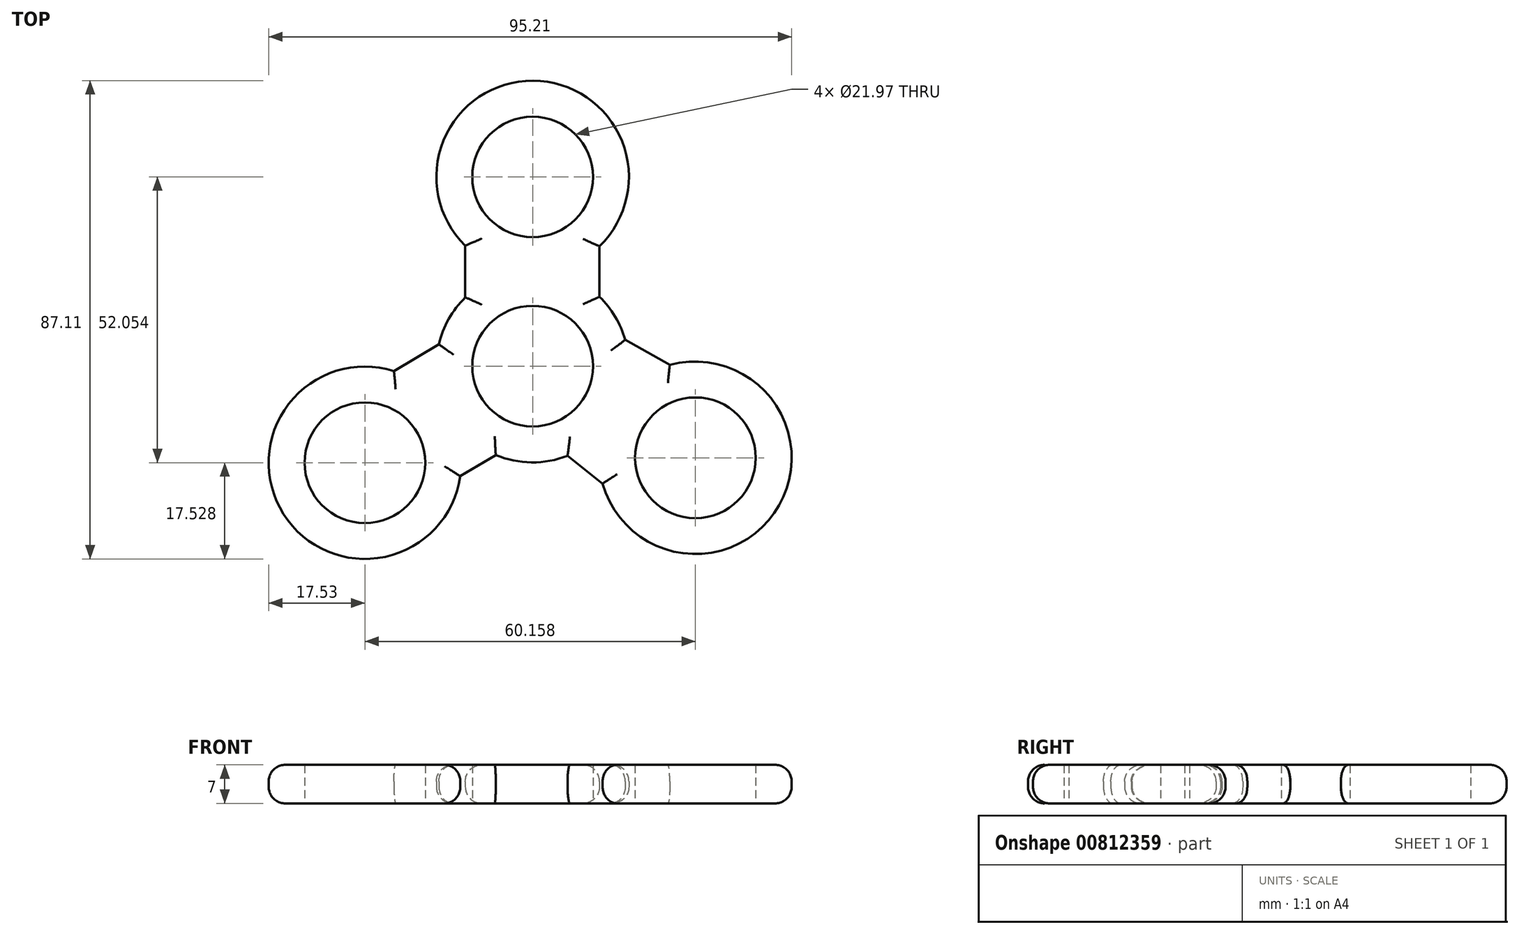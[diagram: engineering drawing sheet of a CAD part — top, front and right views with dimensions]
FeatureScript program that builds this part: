
annotation { "Feature Type Name" : "Feature", "Feature Type Description" : "" }
export const myFeature = defineFeature(function(context is Context, id is Id, definition is map)
    precondition{}
    {
        {
            var Q0;
            Q0=qCreatedBy(makeId("Top.planeOp"),FACE);
            var sketch = newSketch(context, id + "F0", { "sketchPlane" : qUnion([Q0])});
            skCircle(sketch, "E0", {"center": v(0, 0) * mm, "radius": 10.99 * mm});
            skCircle(sketch, "E1", {"center": v(0, 34.46) * mm, "radius": 10.99 * mm});
            skCircle(sketch, "E2", {"center": v(29.63, -16.69) * mm, "radius": 10.99 * mm});
            skCircle(sketch, "E3", {"center": v(-30.53, -17.6) * mm, "radius": 10.99 * mm});
            skArc(sketch, "E4", {"start": v(12.74, -21.39) * mm, "mid": v(44.88, -25.33) * mm, "end": v(24.97, 0.2) * mm});
            skArc(sketch, "E5", {"start": v(-25.26, -0.88) * mm, "mid": v(-45.36, -26.94) * mm, "end": v(-13.18, -20.04) * mm});
            skArc(sketch, "E6", {"start": v(12.16, 21.84) * mm, "mid": v(0.07, 51.99) * mm, "end": v(-12.26, 21.94) * mm});
            skArc(sketch, "E7", {"start": v(-6.71, -16.19) * mm, "mid": v(-0.2, -17.52) * mm, "end": v(6.35, -16.33) * mm});
            skLineSegment(sketch, "E8", {"start": v(-12.26, 21.94) * mm, "end": v(-12.26, 12.52) * mm});
            skLineSegment(sketch, "E9", {"start": v(12.16, 21.84) * mm, "end": v(12.16, 12.62) * mm});
            skLineSegment(sketch, "E10", {"start": v(-25.26, -0.88) * mm, "end": v(-17.07, 3.97) * mm});
            skLineSegment(sketch, "E11", {"start": v(-13.18, -20.04) * mm, "end": v(-6.71, -16.19) * mm});
            skLineSegment(sketch, "E12", {"start": v(16.86, 4.8) * mm, "end": v(24.97, 0.2) * mm});
            skLineSegment(sketch, "E13", {"start": v(6.35, -16.33) * mm, "end": v(12.74, -21.39) * mm});
            skArc(sketch, "E14.trimOffspring", {"start": v(-12.26, 12.52) * mm, "mid": v(-15.28, 8.6) * mm, "end": v(-17.07, 3.97) * mm});
            skArc(sketch, "E15.trimOffspring", {"start": v(16.86, 4.8) * mm, "mid": v(15.03, 9.02) * mm, "end": v(12.16, 12.62) * mm});
            skSolve(sketch);
        }
        {
            var Q0;
            Q0 = qSketchRegion(id + "F0", true);
            extrude(context, id + "F1", {"entities" : qUnion([Q0]), "depth" : 7 * mm, "offsetDistance" : 25.4 * mm});
        }
        {
            var Q0;
            Q0=makeQuery(id+"F1.opExtrude","CAP_EDGE",EDGE,{"disambiguationData":[OSD([sQuery(id+"F0.wireOp",EDGE,"E6")])],"isStart":true});
            var Q1;
            Q1=makeQuery(id+"F1.opExtrude","CAP_EDGE",EDGE,{"disambiguationData":[OSD([sQuery(id+"F0.wireOp",EDGE,"E9")])],"isStart":true});
            var Q2;
            Q2=makeQuery(id+"F1.opExtrude","CAP_EDGE",EDGE,{"disambiguationData":[OSD([sQuery(id+"F0.wireOp",EDGE,"E15.trimOffspring")])],"isStart":true});
            var Q3;
            Q3=makeQuery(id+"F1.opExtrude","CAP_EDGE",EDGE,{"disambiguationData":[OSD([sQuery(id+"F0.wireOp",EDGE,"E12")])],"isStart":true});
            var Q4;
            Q4=makeQuery(id+"F1.opExtrude","CAP_EDGE",EDGE,{"disambiguationData":[OSD([sQuery(id+"F0.wireOp",EDGE,"E4")])],"isStart":true});
            var Q5;
            Q5=makeQuery(id+"F1.opExtrude","CAP_EDGE",EDGE,{"disambiguationData":[OSD([sQuery(id+"F0.wireOp",EDGE,"E13")])],"isStart":true});
            var Q6;
            Q6=makeQuery(id+"F1.opExtrude","CAP_EDGE",EDGE,{"disambiguationData":[OSD([sQuery(id+"F0.wireOp",EDGE,"E7")])],"isStart":true});
            var Q7;
            Q7=makeQuery(id+"F1.opExtrude","CAP_EDGE",EDGE,{"disambiguationData":[OSD([sQuery(id+"F0.wireOp",EDGE,"E11")])],"isStart":true});
            var Q8;
            Q8=makeQuery(id+"F1.opExtrude","CAP_EDGE",EDGE,{"disambiguationData":[OSD([sQuery(id+"F0.wireOp",EDGE,"E5")])],"isStart":true});
            var Q9;
            Q9=makeQuery(id+"F1.opExtrude","CAP_EDGE",EDGE,{"disambiguationData":[OSD([sQuery(id+"F0.wireOp",EDGE,"E10")])],"isStart":true});
            var Q10;
            Q10=makeQuery(id+"F1.opExtrude","CAP_EDGE",EDGE,{"disambiguationData":[OSD([sQuery(id+"F0.wireOp",EDGE,"E14.trimOffspring")])],"isStart":true});
            var Q11;
            Q11=makeQuery(id+"F1.opExtrude","CAP_EDGE",EDGE,{"disambiguationData":[OSD([sQuery(id+"F0.wireOp",EDGE,"E8")])],"isStart":true});
            fillet(context, id + "F2", {"entities" : qUnion([Q0, Q1, Q2, Q3, Q4, Q5, Q6, Q7, Q8, Q9, Q10, Q11]), "radius" : 3 * mm, "tangentPropagation" : true, "allowEdgeOverflow" : false});
        }
        {
            var Q0;
            Q0=makeQuery(id+"F1.opExtrude","CAP_EDGE",EDGE,{"disambiguationData":[OSD([sQuery(id+"F0.wireOp",EDGE,"E6")])],"isStart":false});
            var Q1;
            Q1=makeQuery(id+"F1.opExtrude","CAP_EDGE",EDGE,{"disambiguationData":[OSD([sQuery(id+"F0.wireOp",EDGE,"E8")])],"isStart":false});
            var Q2;
            Q2=makeQuery(id+"F1.opExtrude","CAP_EDGE",EDGE,{"disambiguationData":[OSD([sQuery(id+"F0.wireOp",EDGE,"E14.trimOffspring")])],"isStart":false});
            var Q3;
            Q3=makeQuery(id+"F1.opExtrude","CAP_EDGE",EDGE,{"disambiguationData":[OSD([sQuery(id+"F0.wireOp",EDGE,"E10")])],"isStart":false});
            var Q4;
            Q4=makeQuery(id+"F1.opExtrude","CAP_EDGE",EDGE,{"disambiguationData":[OSD([sQuery(id+"F0.wireOp",EDGE,"E5")])],"isStart":false});
            var Q5;
            Q5=makeQuery(id+"F1.opExtrude","CAP_EDGE",EDGE,{"disambiguationData":[OSD([sQuery(id+"F0.wireOp",EDGE,"E11")])],"isStart":false});
            var Q6;
            Q6=makeQuery(id+"F1.opExtrude","CAP_EDGE",EDGE,{"disambiguationData":[OSD([sQuery(id+"F0.wireOp",EDGE,"E7")])],"isStart":false});
            var Q7;
            Q7=makeQuery(id+"F1.opExtrude","CAP_EDGE",EDGE,{"disambiguationData":[OSD([sQuery(id+"F0.wireOp",EDGE,"E4")])],"isStart":false});
            var Q8;
            Q8=makeQuery(id+"F1.opExtrude","CAP_EDGE",EDGE,{"disambiguationData":[OSD([sQuery(id+"F0.wireOp",EDGE,"E13")])],"isStart":false});
            var Q9;
            Q9=makeQuery(id+"F1.opExtrude","CAP_EDGE",EDGE,{"disambiguationData":[OSD([sQuery(id+"F0.wireOp",EDGE,"E12")])],"isStart":false});
            var Q10;
            Q10=makeQuery(id+"F1.opExtrude","CAP_EDGE",EDGE,{"disambiguationData":[OSD([sQuery(id+"F0.wireOp",EDGE,"E15.trimOffspring")])],"isStart":false});
            var Q11;
            Q11=makeQuery(id+"F1.opExtrude","CAP_EDGE",EDGE,{"disambiguationData":[OSD([sQuery(id+"F0.wireOp",EDGE,"E9")])],"isStart":false});
            fillet(context, id + "F3", {"entities" : qUnion([Q0, Q1, Q2, Q3, Q4, Q5, Q6, Q7, Q8, Q9, Q10, Q11]), "radius" : 3 * mm, "tangentPropagation" : true, "allowEdgeOverflow" : false});
        }
    });
